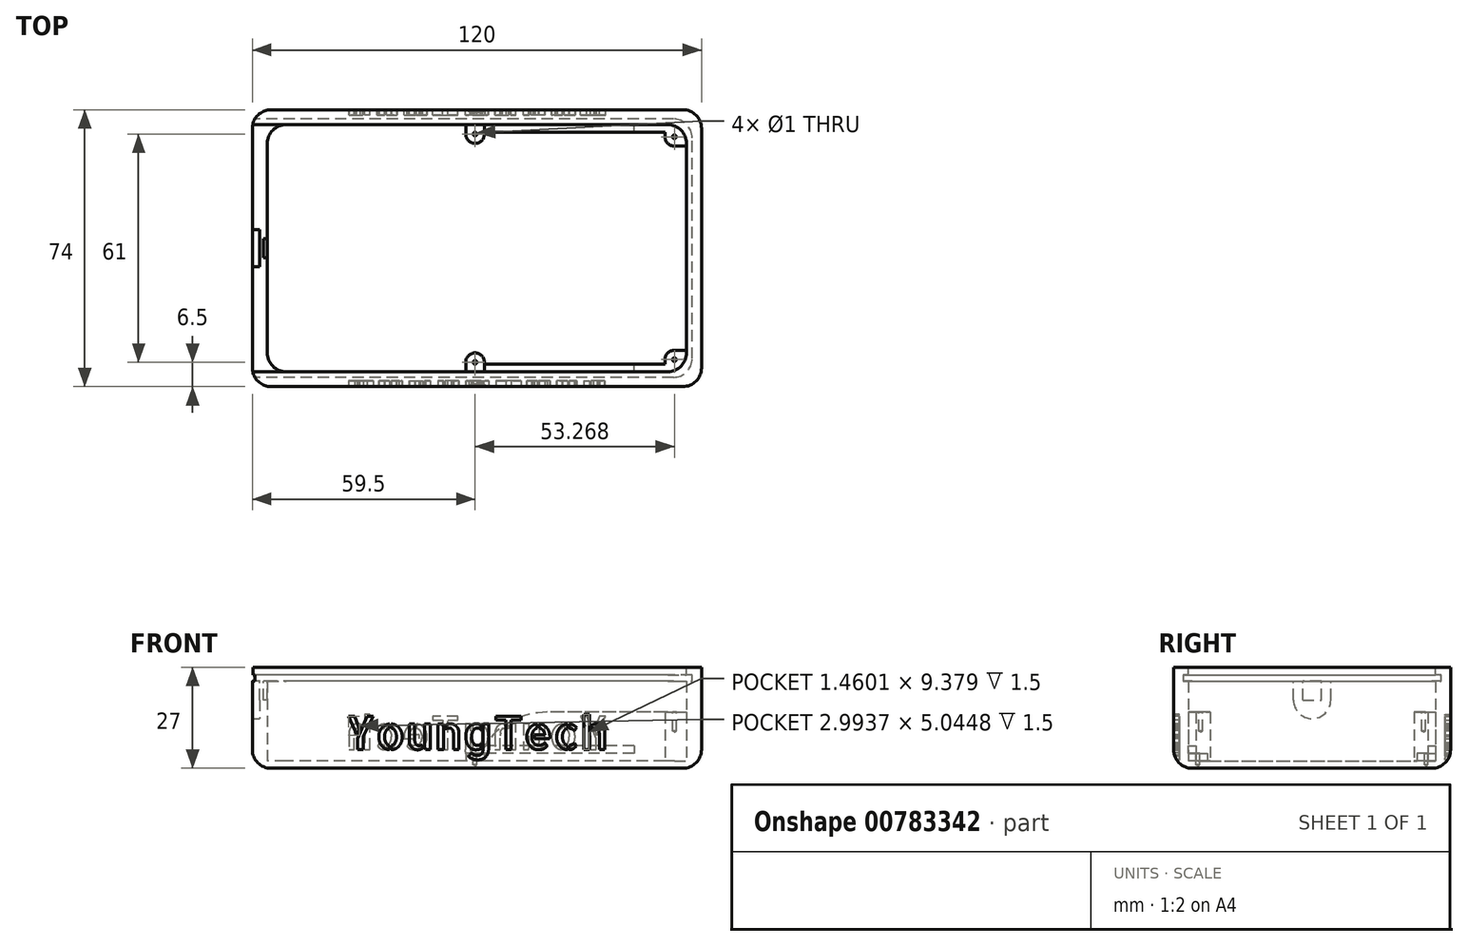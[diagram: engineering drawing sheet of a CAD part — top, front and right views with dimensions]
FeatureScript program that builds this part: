
annotation { "Feature Type Name" : "Feature", "Feature Type Description" : "" }
export const myFeature = defineFeature(function(context is Context, id is Id, definition is map)
    precondition{}
    {
        {
            var Q0;
            Q0=qCreatedBy(makeId("Top.planeOp"),FACE);
            var sketch = newSketch(context, id + "F0", { "sketchPlane" : qUnion([Q0])});
            skLineSegment(sketch, "E0.bottom", {"start": v(60, -37) * mm, "end": v(-60, -37) * mm});
            skLineSegment(sketch, "E0.top", {"start": v(60, 37) * mm, "end": v(-60, 37) * mm});
            skLineSegment(sketch, "E0.left", {"start": v(60, -37) * mm, "end": v(60, 37) * mm});
            skLineSegment(sketch, "E0.right", {"start": v(-60, -37) * mm, "end": v(-60, 37) * mm});
            skPoint(sketch, "E0.middle", {"position": v(0, 0) * mm});
            skSolve(sketch);
        }
        {
            var Q0;
            Q0=qSketchRegion(id+"F0",true);
            extrude(context, id + "F1", {"entities" : qUnion([Q0]), "depth" : 2 * mm, "offsetDistance" : 25 * mm});
        }
        {
            var Q0;
            Q0=makeQuery(id+"F1.opExtrude","CAP_FACE",FACE,{"disambiguationData":[OSD([sQuery(id+"F0.wireOp",EDGE,"E0.bottom"),sQuery(id+"F0.wireOp",EDGE,"E0.top"),sQuery(id+"F0.wireOp",EDGE,"E0.left"),sQuery(id+"F0.wireOp",EDGE,"E0.right")])],"isStart":false});
            var sketch = newSketch(context, id + "F2", { "sketchPlane" : qUnion([Q0])});
            skLineSegment(sketch, "E1.0.0", {"start": v(60, 37) * mm, "end": v(60, -37) * mm});
            skLineSegment(sketch, "E1.0.1", {"start": v(60, -37) * mm, "end": v(-60, -37) * mm});
            skLineSegment(sketch, "E1.0.2", {"start": v(-60, -37) * mm, "end": v(-60, 37) * mm});
            skLineSegment(sketch, "E1.0.3", {"start": v(-60, 37) * mm, "end": v(60, 37) * mm});
            skLineSegment(sketch, "E2.bottom", {"start": v(56, -33) * mm, "end": v(-56, -33) * mm});
            skLineSegment(sketch, "E2.top", {"start": v(56, 33) * mm, "end": v(-56, 33) * mm});
            skLineSegment(sketch, "E2.left", {"start": v(56, -33) * mm, "end": v(56, 33) * mm});
            skLineSegment(sketch, "E2.right", {"start": v(-56, -33) * mm, "end": v(-56, 33) * mm});
            skPoint(sketch, "E2.middle", {"position": v(0, 0) * mm});
            skSolve(sketch);
        }
        {
            var Q0;
            Q0=makeQuery(id+"F2.imprint","IMPRINT",FACE,{"disambiguationData":[TD([[makeQuery(id+"F2.imprint","IMPRINT",EDGE,{"derivedFrom":sQuery(id+"F2.wireOp",EDGE,"E1.0.0")}),1.0]])]});
            extrude(context, id + "F3", {"entities" : qUnion([Q0]), "operationType" : NewBodyOperationType.ADD, "depth" : 25 * mm, "offsetDistance" : 25 * mm});
        }
        {
            var Q0;
            Q0=makeQuery(id+"F3.boolean.opBoolean","MERGE",EDGE,{"derivedFrom":[makeQuery(id+"F1.opExtrude","SWEPT_EDGE",EDGE,{"disambiguationData":[OSD([sQuery(id+"F0.wireOp",EDGE,"E0.top"),sQuery(id+"F0.wireOp",EDGE,"E0.right")])]}),makeQuery(id+"F3.opExtrude","SWEPT_EDGE",EDGE,{"disambiguationData":[OSD([sQuery(id+"F2.wireOp",EDGE,"E1.0.2"),sQuery(id+"F2.wireOp",EDGE,"E1.0.3")])]})]});
            var Q1;
            Q1=makeQuery(id+"F3.boolean.opBoolean","MERGE",EDGE,{"derivedFrom":[makeQuery(id+"F1.opExtrude","SWEPT_EDGE",EDGE,{"disambiguationData":[OSD([sQuery(id+"F0.wireOp",EDGE,"E0.bottom"),sQuery(id+"F0.wireOp",EDGE,"E0.right")])]}),makeQuery(id+"F3.opExtrude","SWEPT_EDGE",EDGE,{"disambiguationData":[OSD([sQuery(id+"F2.wireOp",EDGE,"E1.0.1"),sQuery(id+"F2.wireOp",EDGE,"E1.0.2")])]})]});
            var Q2;
            Q2=makeQuery(id+"F3.boolean.opBoolean","MERGE",EDGE,{"derivedFrom":[makeQuery(id+"F1.opExtrude","SWEPT_EDGE",EDGE,{"disambiguationData":[OSD([sQuery(id+"F0.wireOp",EDGE,"E0.bottom"),sQuery(id+"F0.wireOp",EDGE,"E0.left")])]}),makeQuery(id+"F3.opExtrude","SWEPT_EDGE",EDGE,{"disambiguationData":[OSD([sQuery(id+"F2.wireOp",EDGE,"E1.0.0"),sQuery(id+"F2.wireOp",EDGE,"E1.0.1")])]})]});
            var Q3;
            Q3=makeQuery(id+"F3.opExtrude","SWEPT_EDGE",EDGE,{"disambiguationData":[OSD([sQuery(id+"F2.wireOp",EDGE,"E2.top"),sQuery(id+"F2.wireOp",EDGE,"E2.left")])]});
            var Q4;
            Q4=makeQuery(id+"F3.boolean.opBoolean","MERGE",EDGE,{"derivedFrom":[makeQuery(id+"F1.opExtrude","SWEPT_EDGE",EDGE,{"disambiguationData":[OSD([sQuery(id+"F0.wireOp",EDGE,"E0.top"),sQuery(id+"F0.wireOp",EDGE,"E0.left")])]}),makeQuery(id+"F3.opExtrude","SWEPT_EDGE",EDGE,{"disambiguationData":[OSD([sQuery(id+"F2.wireOp",EDGE,"E1.0.0"),sQuery(id+"F2.wireOp",EDGE,"E1.0.3")])]})]});
            var Q5;
            Q5=makeQuery(id+"F3.opExtrude","SWEPT_EDGE",EDGE,{"disambiguationData":[OSD([sQuery(id+"F2.wireOp",EDGE,"E2.top"),sQuery(id+"F2.wireOp",EDGE,"E2.right")])]});
            var Q6;
            Q6=makeQuery(id+"F3.opExtrude","SWEPT_EDGE",EDGE,{"disambiguationData":[OSD([sQuery(id+"F2.wireOp",EDGE,"E2.bottom"),sQuery(id+"F2.wireOp",EDGE,"E2.right")])]});
            var Q7;
            Q7=makeQuery(id+"F3.opExtrude","SWEPT_EDGE",EDGE,{"disambiguationData":[OSD([sQuery(id+"F2.wireOp",EDGE,"E2.bottom"),sQuery(id+"F2.wireOp",EDGE,"E2.left")])]});
            fillet(context, id + "F4", {"entities" : qUnion([Q0, Q1, Q2, Q3, Q4, Q5, Q6, Q7]), "radius" : 5 * mm, "tangentPropagation" : true, "allowEdgeOverflow" : false});
        }
        {
            var Q0;
            Q0=makeQuery(id+"F3.boolean.opBoolean","MERGE",FACE,{"derivedFrom":[makeQuery(id+"F1.opExtrude","SWEPT_FACE",FACE,{"disambiguationData":[OSD([sQuery(id+"F0.wireOp",EDGE,"E0.right")])]}),makeQuery(id+"F3.opExtrude","SWEPT_FACE",FACE,{"disambiguationData":[OSD([sQuery(id+"F2.wireOp",EDGE,"E1.0.2")])]})]});
            var sketch = newSketch(context, id + "F5", { "sketchPlane" : qUnion([Q0])});
            skLineSegment(sketch, "E3.top", {"start": v(33, 27) * mm, "end": v(-33, 27) * mm});
            skLineSegment(sketch, "E3.left", {"start": v(33, 25) * mm, "end": v(33, 27) * mm});
            skLineSegment(sketch, "E3.right", {"start": v(-33, 25) * mm, "end": v(-33, 27) * mm});
            skLineSegment(sketch, "E4.bottom", {"start": v(34.5, 23.25) * mm, "end": v(-34.5, 23.25) * mm});
            skLineSegment(sketch, "E4.top", {"start": v(34.5, 25) * mm, "end": v(33, 25) * mm});
            skLineSegment(sketch, "E4.left", {"start": v(34.5, 23.25) * mm, "end": v(34.5, 25) * mm});
            skLineSegment(sketch, "E4.right", {"start": v(-34.5, 23.25) * mm, "end": v(-34.5, 25) * mm});
            skLineSegment(sketch, "E5.trimOffspring", {"start": v(-33, 25) * mm, "end": v(-34.5, 25) * mm});
            skLineSegment(sketch, "E6", {"start": v(0, 27) * mm, "end": v(0, 58.06) * mm, "construction": true});
            skSolve(sketch);
        }
        {
            var Q0;
            Q0=qSketchRegion(id+"F5",true);
            extrude(context, id + "F6", {"entities" : qUnion([Q0]), "operationType" : NewBodyOperationType.REMOVE, "oppositeDirection" : true, "depth" : (106 + 10) * mm, "offsetDistance" : 25 * mm});
        }
        {
            var Q0;
            Q0=makeQuery(id+"F6.boolean.opBoolean","COPY",FACE,{"derivedFrom":makeQuery(id+"F6.opExtrude","SWEPT_FACE",FACE,{"disambiguationData":[OSD([sQuery(id+"F5.wireOp",EDGE,"E4.bottom")])]})});
            var sketch = newSketch(context, id + "F7", { "sketchPlane" : qUnion([Q0])});
            skLineSegment(sketch, "E7", {"start": v(0, 0) * mm, "end": v(-56, 0) * mm, "construction": true});
            skLineSegment(sketch, "E8.bottom", {"start": v(-56, 2.5) * mm, "end": v(-57, 2.5) * mm});
            skLineSegment(sketch, "E8.top", {"start": v(-56, -2.5) * mm, "end": v(-57, -2.5) * mm});
            skLineSegment(sketch, "E8.left", {"start": v(-56, 2.5) * mm, "end": v(-56, -2.5) * mm});
            skLineSegment(sketch, "E8.right", {"start": v(-57, 2.5) * mm, "end": v(-57, -2.5) * mm});
            skSolve(sketch);
        }
        {
            var Q0;
            Q0=qSketchRegion(id+"F7",true);
            extrude(context, id + "F8", {"entities" : qUnion([Q0]), "operationType" : NewBodyOperationType.REMOVE, "oppositeDirection" : true, "depth" : 5 * mm, "offsetDistance" : 25 * mm});
        }
        {
            var Q0;
            Q0=makeQuery(id+"F6.boolean.opBoolean","COPY",EDGE,{"derivedFrom":makeQuery(id+"F6.opExtrude","CAP_EDGE",EDGE,{"disambiguationData":[OSD([sQuery(id+"F5.wireOp",EDGE,"E3.left")])],"isStart":false})});
            var Q1;
            Q1=makeQuery(id+"F6.boolean.opBoolean","COPY",EDGE,{"derivedFrom":makeQuery(id+"F6.opExtrude","CAP_EDGE",EDGE,{"disambiguationData":[OSD([sQuery(id+"F5.wireOp",EDGE,"E3.right")])],"isStart":false})});
            fillet(context, id + "F9", {"entities" : qUnion([Q0, Q1]), "radius" : 5 * mm, "tangentPropagation" : true, "allowEdgeOverflow" : false});
        }
        {
            var Q0;
            Q0=makeQuery(id+"F6.boolean.opBoolean","MERGE",FACE,{"derivedFrom":[makeQuery(id+"F3.opExtrude","SWEPT_FACE",FACE,{"disambiguationData":[OSD([sQuery(id+"F2.wireOp",EDGE,"E2.left")])]}),makeQuery(id+"F6.opExtrude","CAP_FACE",FACE,{"disambiguationData":[OSD([sQuery(id+"F5.wireOp",EDGE,"E3.top"),sQuery(id+"F5.wireOp",EDGE,"E3.left"),sQuery(id+"F5.wireOp",EDGE,"E3.right"),sQuery(id+"F5.wireOp",EDGE,"E4.bottom"),sQuery(id+"F5.wireOp",EDGE,"E4.top"),sQuery(id+"F5.wireOp",EDGE,"E4.left"),sQuery(id+"F5.wireOp",EDGE,"E4.right"),sQuery(id+"F5.wireOp",EDGE,"E5.trimOffspring")])],"isStart":false})]});
            var sketch = newSketch(context, id + "F10", { "sketchPlane" : qUnion([Q0])});
            skLineSegment(sketch, "E9.0.2", {"start": v(34.5, 25) * mm, "end": v(-34.5, 25) * mm});
            skLineSegment(sketch, "E9.0.3", {"start": v(-34.5, 25) * mm, "end": v(-34.5, 23.25) * mm});
            skLineSegment(sketch, "E9.0.4", {"start": v(-34.5, 23.25) * mm, "end": v(34.5, 23.25) * mm});
            skLineSegment(sketch, "E9.0.9", {"start": v(34.5, 23.25) * mm, "end": v(34.5, 25) * mm});
            skPoint(sketch, "E10.orphan", {"position": v(-28, 25) * mm});
            skPoint(sketch, "E11.orphan", {"position": v(-28, 23.25) * mm});
            skSolve(sketch);
        }
        {
            var Q0;
            Q0=qSketchRegion(id+"F10",true);
            extrude(context, id + "F11", {"entities" : qUnion([Q0]), "operationType" : NewBodyOperationType.REMOVE, "oppositeDirection" : true, "depth" : 1.5 * mm, "offsetDistance" : 25 * mm});
        }
        {
            var Q0;
            Q0=makeQuery(id+"F11.boolean.opBoolean","COPY",EDGE,{"derivedFrom":makeQuery(id+"F11.opExtrude","CAP_EDGE",EDGE,{"disambiguationData":[OSD([sQuery(id+"F10.wireOp",EDGE,"E9.0.9")])],"isStart":false})});
            var Q1;
            Q1=makeQuery(id+"F11.boolean.opBoolean","COPY",EDGE,{"derivedFrom":makeQuery(id+"F11.opExtrude","CAP_EDGE",EDGE,{"disambiguationData":[OSD([sQuery(id+"F10.wireOp",EDGE,"E9.0.3")])],"isStart":false})});
            fillet(context, id + "F12", {"entities" : qUnion([Q0, Q1]), "radius" : 5 * mm, "tangentPropagation" : true, "allowEdgeOverflow" : false});
        }
        {
            var Q0;
            Q0=makeQuery(id+"F3.boolean.opBoolean","MERGE",FACE,{"derivedFrom":[makeQuery(id+"F1.opExtrude","SWEPT_FACE",FACE,{"disambiguationData":[OSD([sQuery(id+"F0.wireOp",EDGE,"E0.top")])]}),makeQuery(id+"F3.opExtrude","SWEPT_FACE",FACE,{"disambiguationData":[OSD([sQuery(id+"F2.wireOp",EDGE,"E1.0.3")])]})]});
            var sketch = newSketch(context, id + "F13", { "sketchPlane" : qUnion([Q0])});
            skText(sketch, "E12", { "text": "YoungTech", "fontName": "AllertaStencil-Regular.ttf"});
            skLineSegment(sketch, "E13", {"start": v(-55, 0) * mm, "end": v(55, 27) * mm, "construction": true});
            skLineSegment(sketch, "E14", {"start": v(-55, 13.5) * mm, "end": v(55, 13.5) * mm, "construction": true});
            const initialGuessF13  = {"E12": [-0.035, 0.005, 1, 0, 0.0089]};
            skSetInitialGuess(sketch, initialGuessF13);
            skSolve(sketch);
        }
        {
            var Q0;
            Q0=qSketchRegion(id+"F13",true);
            extrude(context, id + "F14", {"entities" : qUnion([Q0]), "operationType" : NewBodyOperationType.REMOVE, "oppositeDirection" : true, "depth" : 1.5 * mm, "offsetDistance" : 25 * mm});
        }
        {
            var Q0;
            Q0=makeQuery(id+"F3.boolean.opBoolean","MERGE",FACE,{"derivedFrom":[makeQuery(id+"F1.opExtrude","SWEPT_FACE",FACE,{"disambiguationData":[OSD([sQuery(id+"F0.wireOp",EDGE,"E0.bottom")])]}),makeQuery(id+"F3.opExtrude","SWEPT_FACE",FACE,{"disambiguationData":[OSD([sQuery(id+"F2.wireOp",EDGE,"E1.0.1")])]})]});
            var sketch = newSketch(context, id + "F15", { "sketchPlane" : qUnion([Q0])});
            skText(sketch, "E15", { "text": "YoungTech", "fontName": "AllertaStencil-Regular.ttf"});
            skLineSegment(sketch, "E16", {"start": v(-55, 27) * mm, "end": v(55, 0) * mm, "construction": true});
            const initialGuessF15  = {"E15": [-0.035, 0.005, 1, 0, 0.0089]};
            skSetInitialGuess(sketch, initialGuessF15);
            skSolve(sketch);
        }
        {
            var Q0;
            Q0=qSketchRegion(id+"F15",true);
            extrude(context, id + "F16", {"entities" : qUnion([Q0]), "operationType" : NewBodyOperationType.REMOVE, "oppositeDirection" : true, "depth" : 1.5 * mm, "offsetDistance" : 25 * mm});
        }
        {
            var Q0;
            Q0=makeQuery(id+"F1.opExtrude","CAP_EDGE",EDGE,{"disambiguationData":[OSD([sQuery(id+"F0.wireOp",EDGE,"E0.bottom")])],"isStart":true});
            fillet(context, id + "F17", {"entities" : qUnion([Q0]), "radius" : 5 * mm, "tangentPropagation" : true, "allowEdgeOverflow" : false});
        }
        {
            var Q0;
            Q0=makeQuery(id+"F3.boolean.opBoolean","MERGE",FACE,{"derivedFrom":[makeQuery(id+"F1.opExtrude","SWEPT_FACE",FACE,{"disambiguationData":[OSD([sQuery(id+"F0.wireOp",EDGE,"E0.right")])]}),makeQuery(id+"F3.opExtrude","SWEPT_FACE",FACE,{"disambiguationData":[OSD([sQuery(id+"F2.wireOp",EDGE,"E1.0.2")])]})]});
            var sketch = newSketch(context, id + "F18", { "sketchPlane" : qUnion([Q0])});
            skLineSegment(sketch, "E17.bottom", {"start": v(5, 13.25) * mm, "end": v(-5, 13.25) * mm});
            skLineSegment(sketch, "E17.top", {"start": v(5, 23.25) * mm, "end": v(-5, 23.25) * mm});
            skLineSegment(sketch, "E17.left", {"start": v(5, 13.25) * mm, "end": v(5, 23.25) * mm});
            skLineSegment(sketch, "E17.right", {"start": v(-5, 13.25) * mm, "end": v(-5, 23.25) * mm});
            skPoint(sketch, "E17.middle", {"position": v(0, 18.25) * mm});
            skSolve(sketch);
        }
        {
            var Q0;
            Q0=qSketchRegion(id+"F18",true);
            extrude(context, id + "F19", {"entities" : qUnion([Q0]), "operationType" : NewBodyOperationType.REMOVE, "oppositeDirection" : true, "depth" : 2 * mm, "offsetDistance" : 25 * mm});
        }
        {
            var Q0;
            Q0=makeQuery(id+"F19.boolean.opBoolean","COPY",EDGE,{"derivedFrom":makeQuery(id+"F19.opExtrude","SWEPT_EDGE",EDGE,{"disambiguationData":[OSD([sQuery(id+"F18.wireOp",EDGE,"E17.bottom"),sQuery(id+"F18.wireOp",EDGE,"E17.right")])]})});
            var Q1;
            Q1=makeQuery(id+"F19.boolean.opBoolean","COPY",EDGE,{"derivedFrom":makeQuery(id+"F19.opExtrude","SWEPT_EDGE",EDGE,{"disambiguationData":[OSD([sQuery(id+"F18.wireOp",EDGE,"E17.bottom"),sQuery(id+"F18.wireOp",EDGE,"E17.left")])]})});
            var Q2;
            Q2=makeQuery(id+"F19.boolean.opBoolean","COPY",EDGE,{"derivedFrom":makeQuery(id+"F19.opExtrude","SWEPT_EDGE",EDGE,{"disambiguationData":[OSD([sQuery(id+"F5.wireOp",EDGE,"E4.bottom"),sQuery(id+"F18.wireOp",EDGE,"E17.top"),sQuery(id+"F18.wireOp",EDGE,"E17.left")])]})});
            var Q3;
            Q3=makeQuery(id+"F19.boolean.opBoolean","COPY",EDGE,{"derivedFrom":makeQuery(id+"F19.opExtrude","SWEPT_EDGE",EDGE,{"disambiguationData":[OSD([sQuery(id+"F5.wireOp",EDGE,"E4.bottom"),sQuery(id+"F18.wireOp",EDGE,"E17.top"),sQuery(id+"F18.wireOp",EDGE,"E17.right")])]})});
            fillet(context, id + "F20", {"entities" : qUnion([Q0, Q1, Q2, Q3]), "radius" : 5 * mm, "tangentPropagation" : true, "allowEdgeOverflow" : false});
        }
        {
            var Q0;
            Q0=makeQuery(id+"F1.opExtrude","CAP_FACE",FACE,{"disambiguationData":[OSD([sQuery(id+"F0.wireOp",EDGE,"E0.bottom"),sQuery(id+"F0.wireOp",EDGE,"E0.top"),sQuery(id+"F0.wireOp",EDGE,"E0.left"),sQuery(id+"F0.wireOp",EDGE,"E0.right")])],"isStart":false});
            var sketch = newSketch(context, id + "F21", { "sketchPlane" : qUnion([Q0])});
            skLineSegment(sketch, "E18", {"start": v(0, 0) * mm, "end": v(65.83, 0) * mm, "construction": true});
            skLineSegment(sketch, "E19.right", {"start": v(2, 33) * mm, "end": v(2, 31) * mm});
            skLineSegment(sketch, "E20.MirrorCS", {"start": v(50.27, -31) * mm, "end": v(2, -31) * mm});
            skLineSegment(sketch, "E21.MirrorCS", {"start": v(2, -33) * mm, "end": v(2, -31) * mm});
            skPoint(sketch, "E22.visualSharp", {"position": v(56, 33) * mm});
            skPoint(sketch, "E23.orphan", {"position": v(56, 31) * mm});
            skArc(sketch, "E24.MirrorCS", {"start": v(56, -28) * mm, "mid": v(54.54, -31.54) * mm, "end": v(51, -33) * mm});
            skLineSegment(sketch, "E25", {"start": v(51, -33) * mm, "end": v(2, -33) * mm});
            skLineSegment(sketch, "E26", {"start": v(51, -28) * mm, "end": v(54.54, -31.54) * mm, "construction": true});
            skArc(sketch, "E27", {"start": v(52.77, -27.27) * mm, "mid": v(51, -28) * mm, "end": v(50.27, -29.77) * mm});
            skLineSegment(sketch, "E28", {"start": v(50.27, -29.77) * mm, "end": v(50.27, -31) * mm});
            skLineSegment(sketch, "E29.MirrorCS", {"start": v(50.27, 29.77) * mm, "end": v(50.27, 31) * mm});
            skArc(sketch, "E30.MirrorCS", {"start": v(52.77, 27.27) * mm, "mid": v(51, 28) * mm, "end": v(50.27, 29.77) * mm});
            skLineSegment(sketch, "E31.MirrorCS", {"start": v(51, 28) * mm, "end": v(54.54, 31.54) * mm, "construction": true});
            skLineSegment(sketch, "E32.MirrorCS", {"start": v(52.77, 27.27) * mm, "end": v(56, 27.27) * mm});
            skLineSegment(sketch, "E33", {"start": v(56, 28) * mm, "end": v(56, 27.27) * mm});
            skLineSegment(sketch, "E34.MirrorCS", {"start": v(50.27, 31) * mm, "end": v(2, 31) * mm});
            skArc(sketch, "E35", {"start": v(51, 33) * mm, "mid": v(54.54, 31.54) * mm, "end": v(56, 28) * mm});
            skLineSegment(sketch, "E36", {"start": v(51, 33) * mm, "end": v(2, 33) * mm});
            skArc(sketch, "E37", {"start": v(-3, 30.5) * mm, "mid": v(-0.5, 28) * mm, "end": v(2, 30.5) * mm});
            skLineSegment(sketch, "E38", {"start": v(-0.5, 30.5) * mm, "end": v(-0.5, 33) * mm, "construction": true});
            skLineSegment(sketch, "E39", {"start": v(-3, 30.5) * mm, "end": v(2, 30.5) * mm, "construction": true});
            skLineSegment(sketch, "E40", {"start": v(2, 31) * mm, "end": v(2, 30.5) * mm});
            skLineSegment(sketch, "E41", {"start": v(-3, 30.5) * mm, "end": v(-3, 33) * mm});
            skLineSegment(sketch, "E42", {"start": v(-3, 33) * mm, "end": v(2, 33) * mm});
            skArc(sketch, "E43.MirrorCS", {"start": v(-3, -30.5) * mm, "mid": v(-0.5, -28) * mm, "end": v(2, -30.5) * mm});
            skLineSegment(sketch, "E44.MirrorCS", {"start": v(-3, -30.5) * mm, "end": v(-3, -33) * mm});
            skLineSegment(sketch, "E45.MirrorCS", {"start": v(-3, -33) * mm, "end": v(2, -33) * mm});
            skLineSegment(sketch, "E46", {"start": v(2, -30.5) * mm, "end": v(2, -31) * mm});
            skLineSegment(sketch, "E47", {"start": v(52.77, -27.27) * mm, "end": v(56, -27.27) * mm});
            skLineSegment(sketch, "E48", {"start": v(56, -27.27) * mm, "end": v(56, -28) * mm});
            skSolve(sketch);
        }
        {
            var Q0;
            Q0=makeQuery(id+"F21.imprint","IMPRINT",FACE,{"disambiguationData":[TD([[makeQuery(id+"F21.imprint","IMPRINT",EDGE,{"derivedFrom":sQuery(id+"F21.wireOp",EDGE,"E20.MirrorCS")}),1.0]])]});
            var Q1;
            Q1=makeQuery(id+"F21.imprint","IMPRINT",FACE,{"disambiguationData":[TD([[makeQuery(id+"F21.imprint","IMPRINT",EDGE,{"derivedFrom":sQuery(id+"F21.wireOp",EDGE,"E19.right")}),1.0]])]});
            extrude(context, id + "F22", {"entities" : qUnion([Q0, Q1]), "operationType" : NewBodyOperationType.ADD, "depth" : 13 * mm, "offsetDistance" : 25 * mm});
        }
        {
            var Q0;
            Q0=makeQuery(id+"F22.opExtrude","SWEPT_FACE",FACE,{"disambiguationData":[OSD([sQuery(id+"F21.wireOp",EDGE,"E19.right")])]});
            var sketch = newSketch(context, id + "F23", { "sketchPlane" : qUnion([Q0])});
            skLineSegment(sketch, "E49.bottom", {"start": v(33, 4) * mm, "end": v(-33, 4) * mm});
            skLineSegment(sketch, "E49.top", {"start": v(33, 6) * mm, "end": v(-33, 6) * mm});
            skLineSegment(sketch, "E49.left", {"start": v(33, 4) * mm, "end": v(33, 6) * mm});
            skLineSegment(sketch, "E49.right", {"start": v(-33, 4) * mm, "end": v(-33, 6) * mm});
            skPoint(sketch, "E49.middle", {"position": v(0, 5) * mm});
            skLineSegment(sketch, "E50", {"start": v(-31, 4) * mm, "end": v(-8, 4) * mm, "construction": true});
            skLineSegment(sketch, "E51", {"start": v(0, 2) * mm, "end": v(0, 5) * mm, "construction": true});
            skSolve(sketch);
        }
        {
            var Q0;
            Q0=qSketchRegion(id+"F23",true);
            extrude(context, id + "F24", {"entities" : qUnion([Q0]), "operationType" : NewBodyOperationType.REMOVE, "oppositeDirection" : true, "depth" : 40 * mm, "offsetDistance" : 25 * mm});
        }
        {
            var Q0;
            Q0=makeQuery(id+"F22.opExtrude","CAP_EDGE",EDGE,{"disambiguationData":[OSD([sQuery(id+"F21.wireOp",EDGE,"E19.right")])],"isStart":false});
            var Q1;
            Q1=makeQuery(id+"F22.opExtrude","CAP_EDGE",EDGE,{"disambiguationData":[OSD([sQuery(id+"F21.wireOp",EDGE,"E21.MirrorCS")])],"isStart":false});
            fillet(context, id + "F25", {"entities" : qUnion([Q0, Q1]), "radius" : 20 * mm, "tangentPropagation" : true, "allowEdgeOverflow" : false});
        }
        {
            var Q0;
            Q0=makeQuery(id+"F22.opExtrude","CAP_FACE",FACE,{"disambiguationData":[OSD([sQuery(id+"F0.wireOp",EDGE,"E0.bottom"),sQuery(id+"F0.wireOp",EDGE,"E0.top"),sQuery(id+"F0.wireOp",EDGE,"E0.left"),sQuery(id+"F0.wireOp",EDGE,"E0.right"),sQuery(id+"F2.wireOp",EDGE,"E2.top"),sQuery(id+"F2.wireOp",EDGE,"E2.left"),sQuery(id+"F21.wireOp",EDGE,"E19.bottom"),sQuery(id+"F21.wireOp",EDGE,"E19.top"),sQuery(id+"F21.wireOp",EDGE,"E19.left"),sQuery(id+"F21.wireOp",EDGE,"E19.right")])],"isStart":false});
            var sketch = newSketch(context, id + "F26", { "sketchPlane" : qUnion([Q0])});
            skLineSegment(sketch, "E52", {"start": v(0, 0) * mm, "end": v(38.34, 0) * mm, "construction": true});
            skSolve(sketch);
        }
        {
            var Q0;
            Q0=makeQuery(id+"F21.imprint","IMPRINT",FACE,{"disambiguationData":[TD([[makeQuery(id+"F21.imprint","IMPRINT",EDGE,{"derivedFrom":sQuery(id+"F21.wireOp",EDGE,"E19.right")}),-1.0]])]});
            var Q1;
            Q1=makeQuery(id+"F21.imprint","IMPRINT",FACE,{"disambiguationData":[TD([[makeQuery(id+"F21.imprint","IMPRINT",EDGE,{"derivedFrom":sQuery(id+"F21.wireOp",EDGE,"E21.MirrorCS")}),1.0]])]});
            extrude(context, id + "F27", {"entities" : qUnion([Q0, Q1]), "operationType" : NewBodyOperationType.ADD, "depth" : 2 * mm, "offsetDistance" : 25 * mm});
        }
        {
            var Q0;
            {var subQ0=sQuery(id+"F21.wireOp",EDGE,"E19.right");var subQ2=sQuery(id+"F23.wireOp",EDGE,"E49.bottom");Q0=makeQuery(id+"F27.boolean.opBoolean","MERGE",FACE,{"derivedFrom":[makeQuery(id+"F24.boolean.opBoolean","COPY",FACE,{"disambiguationData":[TD([makeQuery(id+"F3.opExtrude","SWEPT_FACE",FACE,{"disambiguationData":[OSD([sQuery(id+"F2.wireOp",EDGE,"E2.top")])]})])],"derivedFrom":makeQuery(id+"F24.opExtrude","SWEPT_FACE",FACE,{"disambiguationData":[OSD([subQ2])]})}),makeQuery(id+"F27.opExtrude","CAP_FACE",FACE,{"disambiguationData":[OSD([subQ0,sQuery(id+"F21.wireOp",EDGE,"E37"),sQuery(id+"F21.wireOp",EDGE,"E40"),sQuery(id+"F21.wireOp",EDGE,"E41"),sQuery(id+"F21.wireOp",EDGE,"E42")])],"isStart":false})]});}
            var sketch = newSketch(context, id + "F28", { "sketchPlane" : qUnion([Q0])});
            skPoint(sketch, "E53", {"position": v(-0.5, 30.5) * mm});
            skSolve(sketch);
        }
        {
            var Q0;
            {var subQ0=sQuery(id+"F21.wireOp",EDGE,"E21.MirrorCS");var subQ2=sQuery(id+"F23.wireOp",EDGE,"E49.bottom");Q0=makeQuery(id+"F27.boolean.opBoolean","MERGE",FACE,{"derivedFrom":[makeQuery(id+"F24.boolean.opBoolean","COPY",FACE,{"disambiguationData":[TD([makeQuery(id+"F3.opExtrude","SWEPT_FACE",FACE,{"disambiguationData":[OSD([sQuery(id+"F2.wireOp",EDGE,"E2.bottom")])]})])],"derivedFrom":makeQuery(id+"F24.opExtrude","SWEPT_FACE",FACE,{"disambiguationData":[OSD([subQ2])]})}),makeQuery(id+"F27.opExtrude","CAP_FACE",FACE,{"disambiguationData":[OSD([subQ0,sQuery(id+"F21.wireOp",EDGE,"E43.MirrorCS"),sQuery(id+"F21.wireOp",EDGE,"E44.MirrorCS"),sQuery(id+"F21.wireOp",EDGE,"E45.MirrorCS"),sQuery(id+"F21.wireOp",EDGE,"E46")])],"isStart":false})]});}
            var sketch = newSketch(context, id + "F29", { "sketchPlane" : qUnion([Q0])});
            skPoint(sketch, "E54", {"position": v(-0.5, -30.5) * mm});
            skSolve(sketch);
        }
        {
            var Q0;
            Q0=sQuery(id+"F28.wireOp",VERTEX,"E53");
            var Q1;
            Q1=sQuery(id+"F29.wireOp",VERTEX,"E54");
            var Q2;
            Q2=makeQuery(id+"F1.opExtrude","SWEPT_BODY",BODY,{"disambiguationData":[OSD([sQuery(id+"F0.wireOp",EDGE,"E0.bottom"),sQuery(id+"F0.wireOp",EDGE,"E0.top"),sQuery(id+"F0.wireOp",EDGE,"E0.left"),sQuery(id+"F0.wireOp",EDGE,"E0.right")])]});
            hole(context, id + "F30", {"style" : HoleStyle.SIMPLE, "endStyle" : HoleEndStyle.BLIND, "holeDiameter" : 1 * mm, "majorDiameter" : 5 * mm, "holeDepth" : 3 * mm, "isTappedThrough" : true, "tappedDepth" : 12 * mm, "tapClearance" : 3, "startFromSketch" : true, "locations" : qUnion([Q0, Q1]), "scope" : qUnion([Q2])});
        }
        {
            var Q0;
            {var subQ4=sQuery(id+"F21.wireOp",EDGE,"E29.MirrorCS");Q0=makeQuery(id+"F26.imprint","IMPRINT",FACE,{"disambiguationData":[TD([[makeQuery(id+"F26.imprint","IMPRINT",EDGE,{"derivedFrom":makeQuery(id+"F22.opExtrude","CAP_EDGE",EDGE,{"disambiguationData":[OSD([subQ4])],"isStart":false})}),-1.0]])]});}
            var sketch = newSketch(context, id + "F31", { "sketchPlane" : qUnion([Q0])});
            skLineSegment(sketch, "E55", {"start": v(52.77, 29.77) * mm, "end": v(52.77, -29.77) * mm, "construction": true});
            skSolve(sketch);
        }
        {
            var Q0;
            Q0=sQuery(id+"F31.wireOp",VERTEX,"E55.start");
            var Q1;
            Q1=sQuery(id+"F31.wireOp",VERTEX,"E55.end");
            var Q2;
            Q2=makeQuery(id+"F1.opExtrude","SWEPT_BODY",BODY,{"disambiguationData":[OSD([sQuery(id+"F0.wireOp",EDGE,"E0.bottom"),sQuery(id+"F0.wireOp",EDGE,"E0.top"),sQuery(id+"F0.wireOp",EDGE,"E0.left"),sQuery(id+"F0.wireOp",EDGE,"E0.right")])]});
            hole(context, id + "F32", {"style" : HoleStyle.SIMPLE, "endStyle" : HoleEndStyle.BLIND, "holeDiameter" : 1 * mm, "majorDiameter" : 5 * mm, "holeDepth" : 5 * mm, "isTappedThrough" : true, "tappedDepth" : 12 * mm, "tapClearance" : 3, "startFromSketch" : true, "locations" : qUnion([Q0, Q1]), "scope" : qUnion([Q2])});
        }
    });
